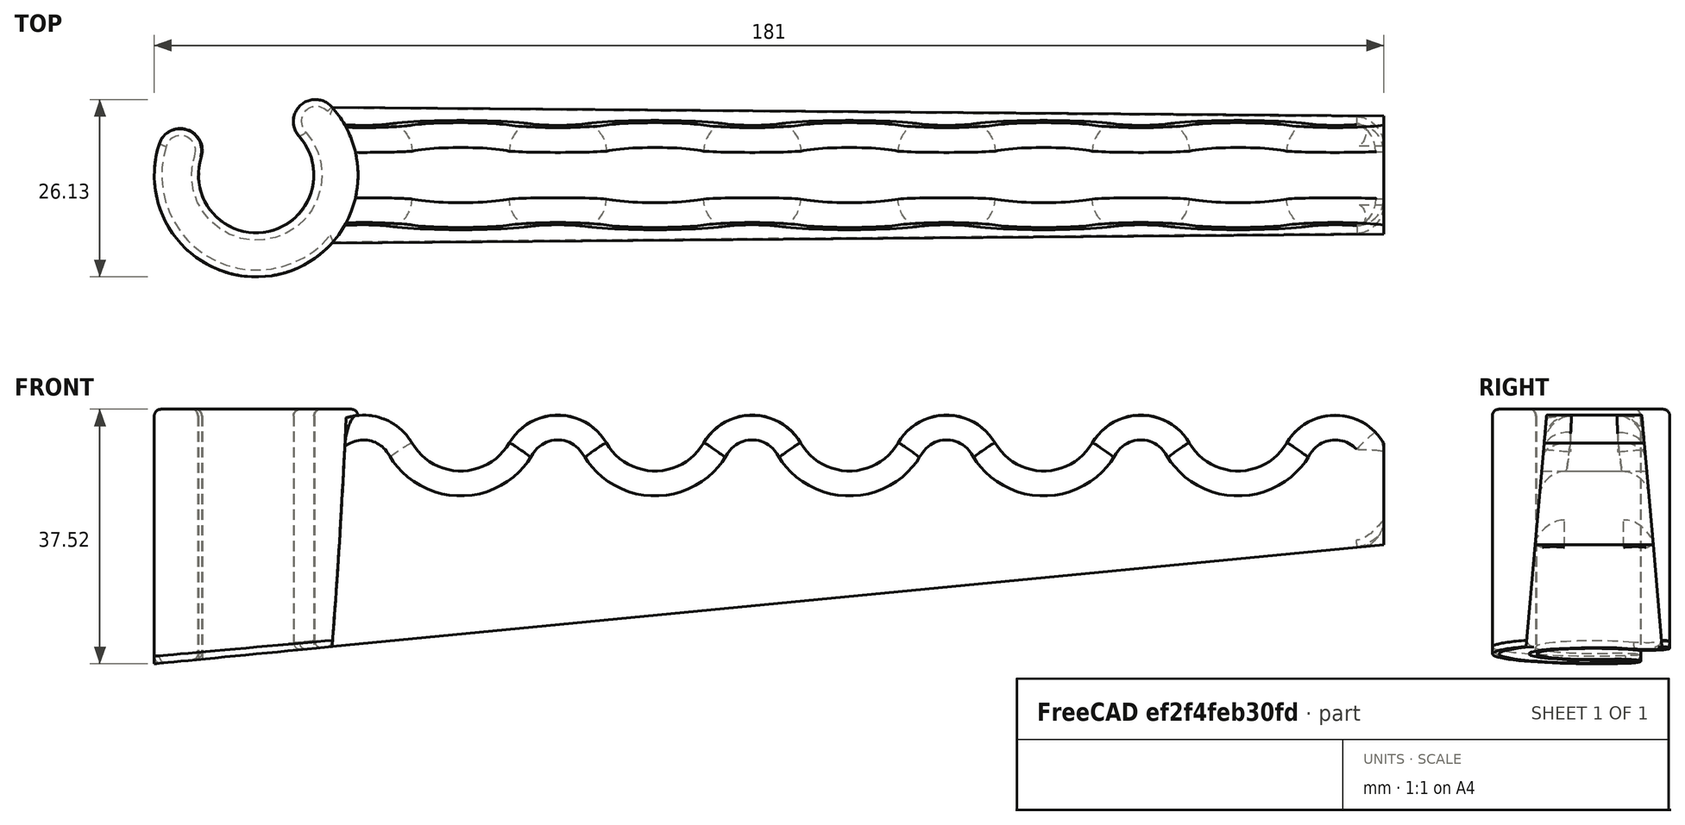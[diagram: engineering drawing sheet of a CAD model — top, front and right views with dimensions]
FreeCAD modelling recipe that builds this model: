
FCSTD DOCUMENT  (FreeCAD 0.18R4 (GitTag))
Label: dryer hook
License: All rights reserved
LicenseURL: http://en.wikipedia.org/wiki/All_rights_reserved
objects: Sketcher::SketchObject×6, PartDesign::Pad×3, PartDesign::Body×3, PartDesign::Plane×2, PartDesign::Pocket×2, Part::Feature×1, PartDesign::Fillet×1, App::Part×1, Part::MultiFuse×1, Part::Cut×1, Part::Fillet×1, Mesh::Feature×1
note: 26 computed .brp shape members not serialized (recipe doc carries the construction recipe); baked Part::Feature solids carry a one-line shape summary decoded from their .brp

FEATURE [Sketcher::SketchObject] Sketch
  MapMode = 5
  Support = -> [XY_Plane]
  sketch-geometry (6):
    g0: ArcOfCircle CenterX=-11 CenterY=0 CenterZ=0 NormalX=0 NormalY=0 NormalZ=1 AngleXU=0 Radius=8.5 StartAngle=2.82935 EndAngle=7.01814
    g1: ArcOfCircle CenterX=-11 CenterY=0 CenterZ=0 NormalX=0 NormalY=0 NormalZ=1 AngleXU=0 Radius=15 StartAngle=2.82935 EndAngle=7.01814
    g2: ArcOfCircle CenterX=-22.1819 CenterY=3.60949 CenterZ=0 NormalX=0 NormalY=0 NormalZ=1 AngleXU=0 Radius=3.25 StartAngle=5.97095 EndAngle=9.11254
    g3: ArcOfCircle CenterX=-2.28316 CenterY=7.87904 CenterZ=0 NormalX=0 NormalY=0 NormalZ=1 AngleXU=0 Radius=3.25 StartAngle=0.734958 EndAngle=3.87655
    g4: LineSegment [constr] StartX=-19.089 StartY=2.61112 StartZ=0 EndX=-25.2747 EndY=4.60786 EndZ=0
    g5: LineSegment [constr] StartX=-4.6942 StartY=5.69973 StartZ=0 EndX=0.127881 EndY=10.0583 EndZ=0
  constraints (16):
    c: Radius(g0) = 8.5
    c: Radius(g1) = 15
    c: Angle(g0) = 4.18879
    c: Angle(g1) = 4.18879
    c: Coincident(g2,g1)
    c: Coincident(g3,g0)
    c: Tangent(g3,g1) = -1.5708
    c: Tangent(g2,g0) = 1.5708
    c: Coincident(g1,g0)
    c: DistanceY(g-1,g0) = 0
    c: Coincident(g4,g0)
    c: Coincident(g4,g1)
    c: Coincident(g5,g0)
    c: Coincident(g5,g1)
    c: PointOnObject(g2,g4)
    c: DistanceX(g0) = -11
FEATURE [PartDesign::Pad] Pad
  Length = 70
  Length2 = 100
  Midplane = true
  Profile = -> Sketch
  Refine = true
  Type = 0
FEATURE [Sketcher::SketchObject] Sketch001
  MapMode = 5
  Placement = pos=(0,0,0) rot=(1,0,0;1.5708rad)
  Support = -> [XZ_Plane002]
  sketch-geometry (16):
    g0: LineSegment StartX=0 StartY=0 StartZ=0 EndX=155 EndY=15 EndZ=0
    g1: LineSegment StartX=0 StartY=0 StartZ=0 EndX=7.99e-14 EndY=30 EndZ=0
    g2: LineSegment StartX=155 StartY=15 StartZ=0 EndX=155 EndY=30 EndZ=0
    g3: LineSegment [constr] StartX=7.99e-14 StartY=30 StartZ=0 EndX=155 EndY=30 EndZ=0
    g4: ArcOfCircle CenterX=147.857 CenterY=25.8761 CenterZ=0 NormalX=0 NormalY=0 NormalZ=1 AngleXU=0 Radius=8.24786 StartAngle=0.523599 EndAngle=2.61799
    g5: ArcOfCircle CenterX=119.254 CenterY=25.87 CenterZ=0 NormalX=0 NormalY=0 NormalZ=1 AngleXU=0 Radius=8.26 StartAngle=0.523599 EndAngle=2.61799
    g6: ArcOfCircle CenterX=90.6407 CenterY=25.87 CenterZ=0 NormalX=0 NormalY=0 NormalZ=1 AngleXU=0 Radius=8.26 StartAngle=0.523599 EndAngle=2.61799
    g7: ArcOfCircle CenterX=104.947 CenterY=34.13 CenterZ=0 NormalX=0 NormalY=0 NormalZ=1 AngleXU=0 Radius=8.26 StartAngle=3.66519 EndAngle=5.75959
    g8: ArcOfCircle CenterX=76.334 CenterY=34.13 CenterZ=0 NormalX=0 NormalY=0 NormalZ=1 AngleXU=0 Radius=8.26 StartAngle=3.66519 EndAngle=5.75959
    g9: ArcOfCircle CenterX=62.0272 CenterY=25.87 CenterZ=0 NormalX=0 NormalY=0 NormalZ=1 AngleXU=0 Radius=8.26 StartAngle=0.523599 EndAngle=2.61799
    g10: ArcOfCircle CenterX=47.7205 CenterY=34.13 CenterZ=0 NormalX=0 NormalY=0 NormalZ=1 AngleXU=0 Radius=8.26 StartAngle=3.66519 EndAngle=5.75959
    g11: ArcOfCircle CenterX=33.4137 CenterY=25.87 CenterZ=0 NormalX=0 NormalY=0 NormalZ=1 AngleXU=0 Radius=8.26 StartAngle=0.523599 EndAngle=2.61799
    g12: ArcOfCircle CenterX=19.107 CenterY=34.13 CenterZ=0 NormalX=0 NormalY=0 NormalZ=1 AngleXU=0 Radius=8.26 StartAngle=3.66519 EndAngle=5.75959
    g13: LineSegment StartX=7.99e-14 StartY=32.592 StartZ=0 EndX=7.99e-14 EndY=30 EndZ=0
    g14: ArcOfCircle CenterX=133.561 CenterY=34.13 CenterZ=0 NormalX=0 NormalY=0 NormalZ=1 AngleXU=0 Radius=8.26 StartAngle=3.66519 EndAngle=5.75959
    g15: ArcOfCircle CenterX=4.80026 CenterY=25.87 CenterZ=0 NormalX=0 NormalY=0 NormalZ=1 AngleXU=0 Radius=8.26 StartAngle=0.523599 EndAngle=2.19093
  constraints (60):
    c: Coincident(g0,g-1)
    c: DistanceX(g0,g0) = 155
    c: Coincident(g1,g0)
    c: PointOnObject(g1,g-2)
    c: DistanceY(g1,g1) = 30
    c: Vertical(g2)
    c: DistanceY(g2,g2) = 15
    c: Coincident(g3,g1)
    c: Coincident(g3,g2)
    c: Coincident(g4,g2)
    c: PointOnObject(g4,g3)
    c: DistanceX(g4,g2) = 14.2857
    c: PointOnObject(g5,g3)
    c: PointOnObject(g5,g3)
    c: Coincident(g2,g0)
    c: Coincident(g6,g7)
    c: Equal(g6,g7)
    c: Parallel(g5,g6) = 2.0944
    c: PointOnObject(g7,g3)
    c: Coincident(g9,g8)
    c: Equal(g9,g8)
    c: PointOnObject(g9,g3)
    c: Coincident(g11,g10)
    c: Equal(g11,g10)
    c: PointOnObject(g11,g3)
    c: Coincident(g7,g5)
    c: Coincident(g8,g6)
    c: Coincident(g10,g9)
    c: PointOnObject(g9,g3)
    c: PointOnObject(g6,g3)
    c: Equal(g8,g7)
    c: Equal(g8,g10)
    c: Angle(g7) = 2.0944
    c: Angle(g6) = 2.0944
    c: Angle(g8) = 2.0944
    c: Angle(g9) = 2.0944
    c: Angle(g10) = 2.0944
    c: Angle(g11) = 2.0944
    c: PointOnObject(g11,g3)
    c: Radius(g7) = 8.26
    c: Angle(g5) = 2.0944
    c: Angle(g4) = 2.0944
    c: Parallel(g10,g12) = 2.0944
    c: PointOnObject(g12,g3)
    c: Coincident(g12,g11)
    c: Angle(g12) = 2.0944
    c: Radius(g12) = 8.26
    c: Coincident(g13,g1)
    c: Vertical(g13)
    c: Parallel(g7,g14) = 2.0944
    c: Equal(g7,g14) = 8.26
    c: Coincident(g14,g5)
    c: Radius(g5) = 8.26
    c: Coincident(g14,g4)
    c: Angle(g14) = 2.0944
    c: Horizontal(g3)
    c: Parallel(g11,g15) = 2.0944
    c: Coincident(g15,g12)
    c: Radius(g15) = 8.26
    c: Coincident(g13,g15)
FEATURE [PartDesign::Pad] Pad001
  Length = 20
  Length2 = 100
  Midplane = true
  Placement = pos=(0,0,0) rot=(1,0,0;1.5708rad)
  Profile = -> Sketch001
  Refine = true
  Type = 0
FEATURE [PartDesign::Plane] DatumPlane
  Length = 54.4474
  MapMode = 5
  Placement = pos=(1e-16,0,0) rot=(-0.707107,0,0.707107;3.14159rad)
  ResizeMode = 0
  Support = -> [Pad001]
  Width = 70.6226
FEATURE [Sketcher::SketchObject] Sketch002
  ExternalGeometry = -> [Pad001]
  MapMode = 5
  Placement = pos=(1e-16,0,0) rot=(-0.707107,0,0.707107;3.14159rad)
  Support = -> [DatumPlane]
  sketch-geometry (4):
    g0: LineSegment StartX=-34.1442 StartY=7 StartZ=0 EndX=0 EndY=10 EndZ=0
    g1: LineSegment [constr] StartX=0 StartY=0 StartZ=0 EndX=-40 EndY=0 EndZ=0
    g2: LineSegment StartX=-34.1442 StartY=7 StartZ=0 EndX=-32.592 EndY=10 EndZ=0
    g3: LineSegment StartX=-32.592 StartY=10 StartZ=0 EndX=0 EndY=10 EndZ=0
  constraints (7):
    c: Coincident(g1,g-1)
    c: PointOnObject(g1,g-1)
    c: DistanceX(g1,g-1) = 40
    c: Coincident(g2,g0)
    c: Coincident(g2,g-4)
    c: Coincident(g3,g0)
    c: Coincident(g3,g2)
FEATURE [PartDesign::Pocket] Pocket
  BaseFeature = -> Pad001
  Length = 5
  Length2 = 100
  Placement = pos=(0,0,0) rot=(1,0,0;1.5708rad)
  Profile = -> Sketch002
  Refine = true
  Type = 1
FEATURE [Sketcher::SketchObject] Sketch003
  ExternalGeometry = -> [Pocket]
  MapMode = 5
  Placement = pos=(1e-16,0,0) rot=(-0.707107,0,0.707107;3.14159rad)
  Support = -> [DatumPlane]
  sketch-geometry (6):
    g0: LineSegment [constr] StartX=-22.91 StartY=0 StartZ=0 EndX=-39.6936 EndY=0 EndZ=0
    g1: LineSegment [constr] StartX=-34.1442 StartY=7 StartZ=0 EndX=-34.1442 EndY=-7 EndZ=0
    g2: LineSegment StartX=-34.1442 StartY=-7 StartZ=0 EndX=-34.1442 EndY=-10 EndZ=0
    g3: LineSegment StartX=-34.1442 StartY=-10 StartZ=0 EndX=-2.27628e-05 EndY=-10 EndZ=0
    g4: LineSegment StartX=-2.27628e-05 StartY=-10 StartZ=0 EndX=-34.1442 EndY=-7 EndZ=0
    g5: LineSegment [constr] StartX=-2.27628e-05 StartY=10 StartZ=0 EndX=-2.27628e-05 EndY=-10 EndZ=0
  constraints (10):
    c: PointOnObject(g0,g-1)
    c: PointOnObject(g0,g-1)
    c: Symmetric(g1,g1,g0)
    c: Coincident(g2,g3)
    c: Coincident(g3,g4)
    c: Coincident(g4,g2)
    c: Symmetric(g5,g5,g0)
    c: Coincident(g5,g3)
    c: Coincident(g2,g1)
    c: Block(g0)
FEATURE [PartDesign::Pocket] Pocket001
  BaseFeature = -> Pocket
  Length = 5
  Length2 = 100
  Placement = pos=(0,0,0) rot=(1,0,0;1.5708rad)
  Profile = -> Sketch003
  Refine = true
  Type = 1
FEATURE [PartDesign::Plane] DatumPlane001
  Length = 246.096
  MapMode = 5
  Placement = pos=(0,0,0) rot=(0.998837,0,0.048218;3.14159rad)
  ResizeMode = 0
  Support = -> [Pocket001]
  Width = 83.4934
FEATURE [Sketcher::SketchObject] Sketch004
  MapMode = 5
  Placement = pos=(0,0,0) rot=(0.998837,0,0.048218;3.14159rad)
  Support = -> [DatumPlane001]
  sketch-geometry (4):
    g0: LineSegment StartX=-35.7681 StartY=29.6369 StartZ=0 EndX=184.936 EndY=29.6369 EndZ=0
    g1: LineSegment StartX=184.936 StartY=29.6369 StartZ=0 EndX=184.936 EndY=-30.6682 EndZ=0
    g2: LineSegment StartX=184.936 StartY=-30.6682 StartZ=0 EndX=-35.7681 EndY=-30.6682 EndZ=0
    g3: LineSegment StartX=-35.7681 StartY=-30.6682 StartZ=0 EndX=-35.7681 EndY=29.6369 EndZ=0
  constraints (8):
    c: Coincident(g0,g1)
    c: Coincident(g1,g2)
    c: Coincident(g2,g3)
    c: Coincident(g3,g0)
    c: Horizontal(g0)
    c: Horizontal(g2)
    c: Vertical(g1)
    c: Vertical(g3)
FEATURE [PartDesign::Body] Body001
  Group = -> [Sketch001,Pad001,DatumPlane,Sketch002,Pocket,Sketch003,Pocket001,DatumPlane001,Sketch004]
  Origin = -> Origin002
  Tip = -> Pocket001
FEATURE [Sketcher::SketchObject] CopySketch004
  Placement = pos=(0,0,0) rot=(0.998837,0,0.048218;3.14159rad)
  sketch-geometry (4):
    g0: LineSegment StartX=-35.7681 StartY=29.6369 StartZ=0 EndX=184.936 EndY=29.6369 EndZ=0
    g1: LineSegment StartX=184.936 StartY=29.6369 StartZ=0 EndX=184.936 EndY=-30.6682 EndZ=0
    g2: LineSegment StartX=184.936 StartY=-30.6682 StartZ=0 EndX=-35.7681 EndY=-30.6682 EndZ=0
    g3: LineSegment StartX=-35.7681 StartY=-30.6682 StartZ=0 EndX=-35.7681 EndY=29.6369 EndZ=0
  constraints (8):
    c: Coincident(g0,g1)
    c: Coincident(g1,g2)
    c: Coincident(g2,g3)
    c: Coincident(g3,g0)
    c: Horizontal(g0)
    c: Horizontal(g2)
    c: Vertical(g1)
    c: Vertical(g3)
FEATURE [PartDesign::Pad] Pad002
  Length = 50
  Length2 = 100
  Placement = pos=(0,0,0) rot=(0.998837,0,0.048218;3.14159rad)
  Profile = -> CopySketch004
  Refine = true
  Type = 0
FEATURE [PartDesign::Body] Body002
  Group = -> [CopySketch004,Pad002]
  Origin = -> Origin003
  Tip = -> Pad002
FEATURE [Part::Feature] Cut_solid  label="Cut (Solid)"
  shape: bbox 181.5 x 26.82 x 37.57 mm, 25 faces (baked)
FEATURE [PartDesign::Fillet] Fillet
  Base = -> Pad [Face6,Face5]
  BaseFeature = -> Pad
  Radius = 1
FEATURE [PartDesign::Body] Body
  Group = -> [Sketch,Pad,Fillet]
  Origin = -> Origin
  Tip = -> Fillet
FEATURE [App::Part] Part
  Group = -> [Body,Body001,Body002]
  Origin = -> Origin001
FEATURE [Part::MultiFuse] Fusion
  Refine = true
  Shapes = -> [Body,Body001]
FEATURE [Part::Cut] Cut
  Base = -> Fusion
  Refine = true
  Tool = -> Body002
FEATURE [Part::Fillet] Fillet001
  Base = -> Cut_solid
  Edges = 33 edges: [Edge1 r=1,Edge5 r=1,Edge12 r=1,Edge15 r=1,Edge21 r=1,Edge22 r=1,Edge23 r=4,Edge24 r=4,Edge25 r=4,Edge26 r=4,Edge27 r=4,Edge28 r=4,Edge29 r=4,Edge30 r=4,Edge31 r=4,Edge32 r=4,Edge33 r=4,Edge34 r=4,Edge35 r=4,Edge43 r=4,Edge44 r=4,Edge45 r=4,Edge46 r=4,Edge47 r=4,Edge48 r=4,Edge49 r=4,Edge50 r=4,Edge51 r=4,Edge52 r=4,Edge53 r=4,Edge54 r=1,Edge55 r=4,Edge56 r=4]
FEATURE [Mesh::Feature] Mesh  label="Fillet001 (Meshed)"
